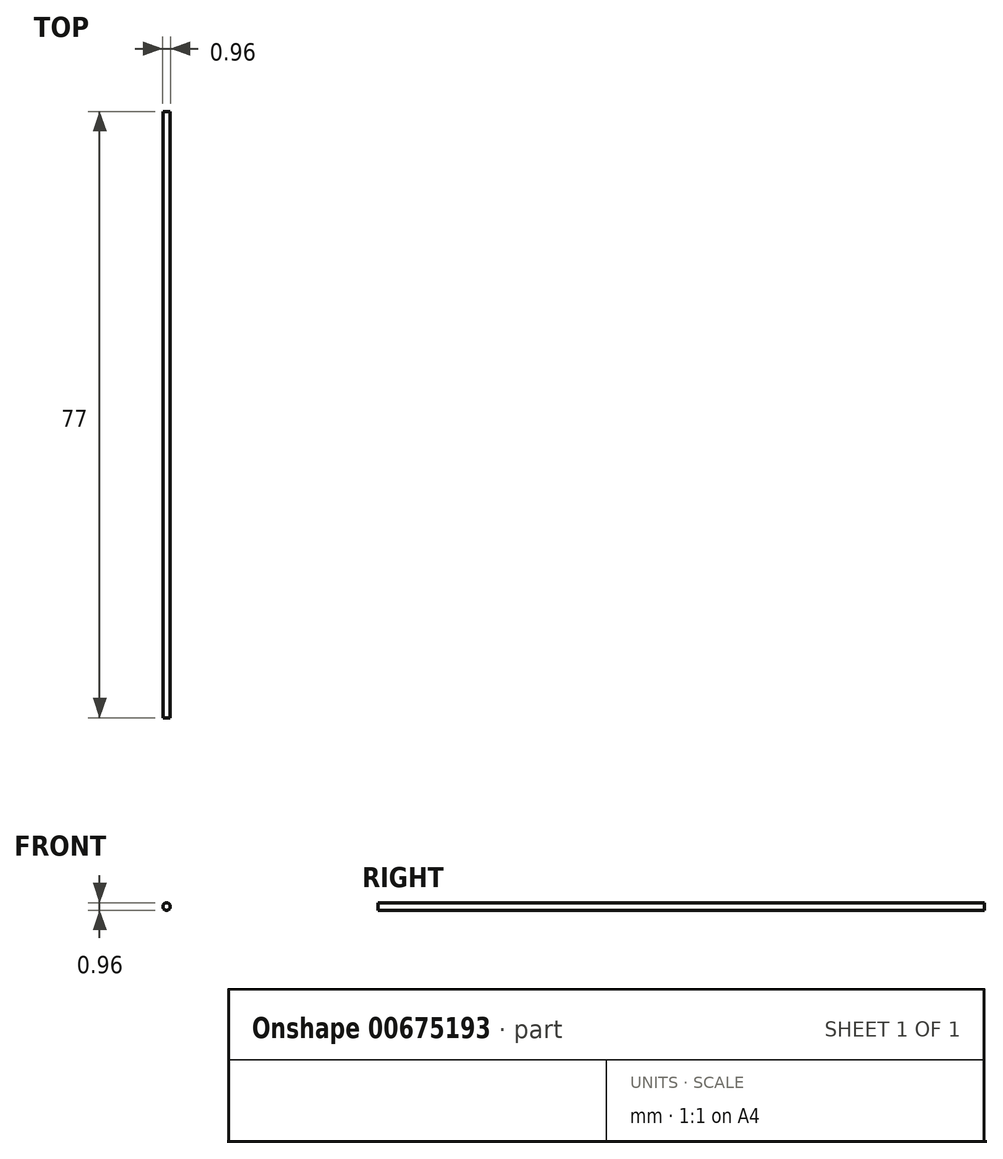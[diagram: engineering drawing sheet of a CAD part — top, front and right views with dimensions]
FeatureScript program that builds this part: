
annotation { "Feature Type Name" : "Feature", "Feature Type Description" : "" }
export const myFeature = defineFeature(function(context is Context, id is Id, definition is map)
    precondition{}
    {
        {
            var Q0;
            Q0=qCreatedBy(makeId("Front.planeOp"),FACE);
            var sketch = newSketch(context, id + "F0", { "sketchPlane" : qUnion([Q0])});
            skCircle(sketch, "E0", {"center": v(0, 0) * mm, "radius": 0.48 * mm});
            skSolve(sketch);
        }
        {
            var Q0;
            Q0 = qSketchRegion(id + "F0", true);
            extrude(context, id + "F1", {"entities" : qUnion([Q0]), "depth" : 77 * mm, "offsetDistance" : 25 * mm});
        }
    });
